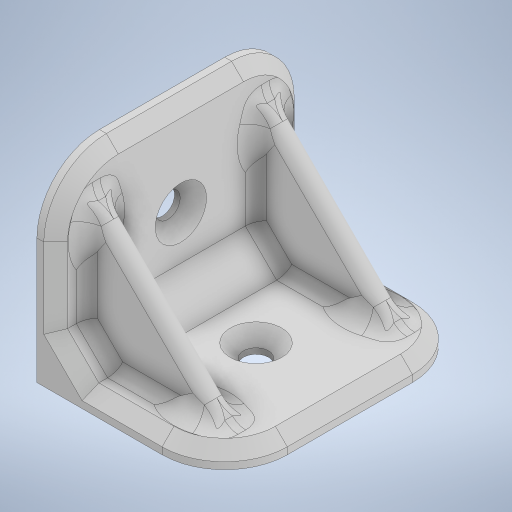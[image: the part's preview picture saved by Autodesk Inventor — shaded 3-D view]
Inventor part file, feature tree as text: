
AUTODESK INVENTOR PART (.ipt)
format: ipt  version: 2024.1 (Build 281209000, 209)  size: 785,408 bytes
history: native  units: in
note: dims shown in document units (in); Inventor stores cm internally (conversion verified against a paired STEP export)
features: sketch x7, extrude x5, fillet x4, plane x2, chamfer x2, hole x2, other x1, mirror x1, projected_geometry x1
ambient origin geometry x8: Origin, YZ Plane, XZ Plane, XY Plane, X Axis, Y Axis, Z Axis, Center Point
bodies: Body1 (feature_tree)
feature tree (25):
  other  "bracket"
  extrude  "Extrusion1"  Depth=1.1811in
  extrude  "Extrusion2"  Depth=0.1181in
  extrude  "Extrusion3"  Depth=0.1575in
  extrude  "Extrusion4"  Depth=0.7874in
  plane  "Work Plane1"
  extrude  "Extrusion5"  Depth=0.5906in
  plane  "Work Plane3"
  fillet  "Fillet1"  Radius=1.063in
  chamfer  "Chamfer1"  Distance=0.5906in
  fillet  "Fillet2"  Radius=1.5748in
  fillet  "Fillet3"  Radius=0.7874in
  chamfer  "Chamfer2"  Distance=1.063in
  sketch  "Sketch8"  dims[d16=0.1575in]
  sketch  "Sketch9"  dims[d17=1.1811in d18=0.5906in d19=1.5748in d20=0.7874in d21=1.063in d22=0.0in d27=-0.1969in d28=0.1969in d29=0.1969in d30=0.1181in d31=0.0in d32=0.3937in d33=0.1969in d34=0.0787in d35=45.0deg d36=0.0669in d37=0.0591in d38=0.0748in d39=0.0787in d40=45.0deg d41=0.1575in d42=0.2362in d43=0.3228in d44=0.0787in d45=90.0deg d46=0.315in d47=0.8108in d48=0.1575in d49=0.2362in d50=0.3228in d51=0.0787in d52=90.0deg d53=0.315in d54=0.8108in d55=0.1181in]
  hole  "Hole1"  [1 undecoded]
  hole  "Hole2"  [1 undecoded]
  fillet  "Fillet4"  Radius=0.1969in
  mirror  "Mirror1"
  sketch  "Sketch1"  dims[d0=1.5748in d1=1.1811in]
  sketch  "Sketch2"  dims[d2=0.1181in d3=0.0in d4=0.1181in]
  sketch  "Sketch3"  dims[d5=1.063in d6=0.0in d7=0.1575in]
  sketch  "Sketch4"  dims[d8=1.5748in d9=0.7874in]
  sketch  "Sketch7"  dims[d12=1.1811in d13=0.5906in d14=1.063in d15=0.0in]
  projected_geometry  "Projected Loop1"
note: 2 required parameter values undecoded (feature->parameter linkage not recoverable at this tier; creation-order binding heuristic only, values carry confidence <= 0.55)
